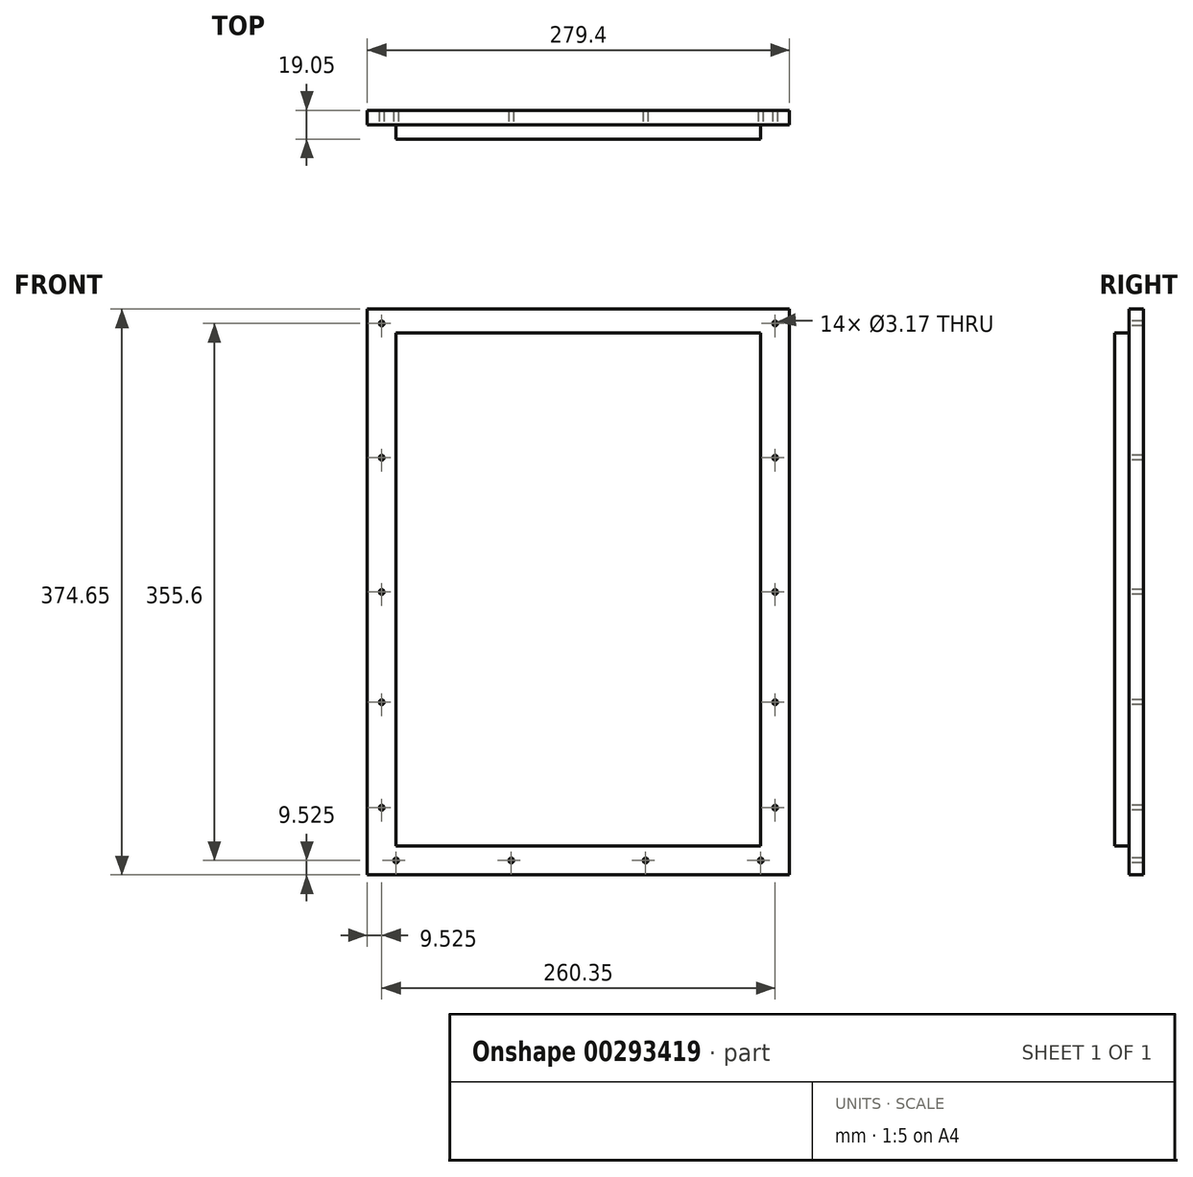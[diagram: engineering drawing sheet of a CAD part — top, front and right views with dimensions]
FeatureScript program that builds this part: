
annotation { "Feature Type Name" : "Feature", "Feature Type Description" : "" }
export const myFeature = defineFeature(function(context is Context, id is Id, definition is map)
    precondition{}
    {
        {
            var Q0;
            Q0=qCreatedBy(makeId("Front.planeOp"),FACE);
            var sketch = newSketch(context, id + "F0", { "sketchPlane" : qUnion([Q0])});
            skLineSegment(sketch, "E0.bottom", {"start": v(-120.65, 177.8) * mm, "end": v(120.65, 177.8) * mm});
            skLineSegment(sketch, "E0.top", {"start": v(-120.65, -177.8) * mm, "end": v(120.65, -177.8) * mm});
            skLineSegment(sketch, "E0.left", {"start": v(-120.65, 177.8) * mm, "end": v(-120.65, -177.8) * mm});
            skLineSegment(sketch, "E0.right", {"start": v(120.65, 177.8) * mm, "end": v(120.65, -177.8) * mm});
            skPoint(sketch, "E0.middle", {"position": v(0, 0) * mm});
            skLineSegment(sketch, "E1.bottom", {"start": v(-120.65, 177.8) * mm, "end": v(-139.7, 177.8) * mm});
            skLineSegment(sketch, "E2.bottom", {"start": v(120.65, 177.8) * mm, "end": v(139.7, 177.8) * mm});
            skLineSegment(sketch, "E3.top", {"start": v(-139.7, -196.85) * mm, "end": v(139.7, -196.85) * mm});
            skLineSegment(sketch, "E4", {"start": v(-139.7, 177.8) * mm, "end": v(-139.7, -196.85) * mm});
            skLineSegment(sketch, "E5", {"start": v(139.7, 177.8) * mm, "end": v(139.7, -196.85) * mm});
            skLineSegment(sketch, "E6", {"start": v(-120.65, 161.93) * mm, "end": v(120.65, 161.93) * mm});
            skLineSegment(sketch, "E7", {"start": v(-130.18, 177.8) * mm, "end": v(-130.18, -196.85) * mm, "construction": true});
            skLineSegment(sketch, "E8", {"start": v(130.18, 177.8) * mm, "end": v(130.18, -196.85) * mm, "construction": true});
            skLineSegment(sketch, "E9", {"start": v(-139.7, -187.32) * mm, "end": v(139.7, -187.32) * mm, "construction": true});
            skLineSegment(sketch, "E10", {"start": v(-139.7, 168.28) * mm, "end": v(139.7, 168.28) * mm, "construction": true});
            skLineSegment(sketch, "E11", {"start": v(-44.45, 177.8) * mm, "end": v(-44.45, -196.85) * mm, "construction": true});
            skLineSegment(sketch, "E12", {"start": v(44.45, 177.8) * mm, "end": v(44.45, -196.85) * mm, "construction": true});
            skCircle(sketch, "E13", {"center": v(-120.65, -187.32) * mm, "radius": 1.59 * mm});
            skCircle(sketch, "E14", {"center": v(-44.45, -187.32) * mm, "radius": 1.59 * mm});
            skCircle(sketch, "E15", {"center": v(44.45, -187.32) * mm, "radius": 1.59 * mm});
            skCircle(sketch, "E16", {"center": v(120.65, -187.32) * mm, "radius": 1.59 * mm});
            skCircle(sketch, "E17", {"center": v(130.18, 168.28) * mm, "radius": 1.59 * mm});
            skCircle(sketch, "E18", {"center": v(-130.18, 168.28) * mm, "radius": 1.59 * mm});
            skLineSegment(sketch, "E19", {"start": v(139.7, -9.53) * mm, "end": v(-139.7, -9.52) * mm, "construction": true});
            skLineSegment(sketch, "E20", {"start": v(-139.7, 79.38) * mm, "end": v(139.7, 79.38) * mm, "construction": true});
            skLineSegment(sketch, "E21", {"start": v(-139.7, -82.55) * mm, "end": v(139.7, -82.55) * mm, "construction": true});
            skCircle(sketch, "E22", {"center": v(130.18, -82.55) * mm, "radius": 1.59 * mm});
            skCircle(sketch, "E23", {"center": v(130.18, -9.53) * mm, "radius": 1.59 * mm});
            skCircle(sketch, "E24", {"center": v(130.18, 79.38) * mm, "radius": 1.59 * mm});
            skCircle(sketch, "E25", {"center": v(-130.18, 79.38) * mm, "radius": 1.59 * mm});
            skCircle(sketch, "E26", {"center": v(-130.18, -9.53) * mm, "radius": 1.59 * mm});
            skCircle(sketch, "E27", {"center": v(-130.18, -82.55) * mm, "radius": 1.59 * mm});
            skLineSegment(sketch, "E28", {"start": v(-139.7, -152.4) * mm, "end": v(139.7, -152.4) * mm, "construction": true});
            skCircle(sketch, "E29", {"center": v(130.18, -152.4) * mm, "radius": 1.59 * mm});
            skCircle(sketch, "E30", {"center": v(-130.18, -152.4) * mm, "radius": 1.59 * mm});
            skSolve(sketch);
        }
        {
            var Q0;
            {var subQ6=sQuery(id+"F0.wireOp",EDGE,"E0.top");Q0=makeQuery(id+"F0.imprint","IMPRINT",FACE,{"disambiguationData":[TD([[makeQuery(id+"F0.imprint","IMPRINT",EDGE,{"derivedFrom":subQ6}),-1.0]])]});}
            var Q1;
            {var subQ0=sQuery(id+"F0.wireOp",EDGE,"E0.top");Q1=makeQuery(id+"F0.imprint","IMPRINT",FACE,{"disambiguationData":[TD([[makeQuery(id+"F0.imprint","IMPRINT",EDGE,{"derivedFrom":subQ0}),1.0]])]});}
            var Q2;
            {var subQ0=sQuery(id+"F0.wireOp",EDGE,"E0.bottom");Q2=makeQuery(id+"F0.imprint","IMPRINT",FACE,{"disambiguationData":[TD([[makeQuery(id+"F0.imprint","IMPRINT",EDGE,{"derivedFrom":subQ0}),-1.0]])]});}
            extrude(context, id + "F1", {"entities" : qUnion([Q0, Q1, Q2]), "oppositeDirection" : true, "depth" : 19.05 * mm});
        }
        {
            var Q0;
            {var subQ6=sQuery(id+"F0.wireOp",EDGE,"E0.top");Q0=makeQuery(id+"F0.imprint","IMPRINT",FACE,{"disambiguationData":[TD([[makeQuery(id+"F0.imprint","IMPRINT",EDGE,{"derivedFrom":subQ6}),-1.0]])]});}
            var Q1;
            {var subQ0=sQuery(id+"F0.wireOp",EDGE,"E0.bottom");Q1=makeQuery(id+"F0.imprint","IMPRINT",FACE,{"disambiguationData":[TD([[makeQuery(id+"F0.imprint","IMPRINT",EDGE,{"derivedFrom":subQ0}),-1.0]])]});}
            extrude(context, id + "F2", {"entities" : qUnion([Q0, Q1]), "operationType" : NewBodyOperationType.REMOVE, "oppositeDirection" : true, "depth" : 9.52 * mm});
        }
    });
